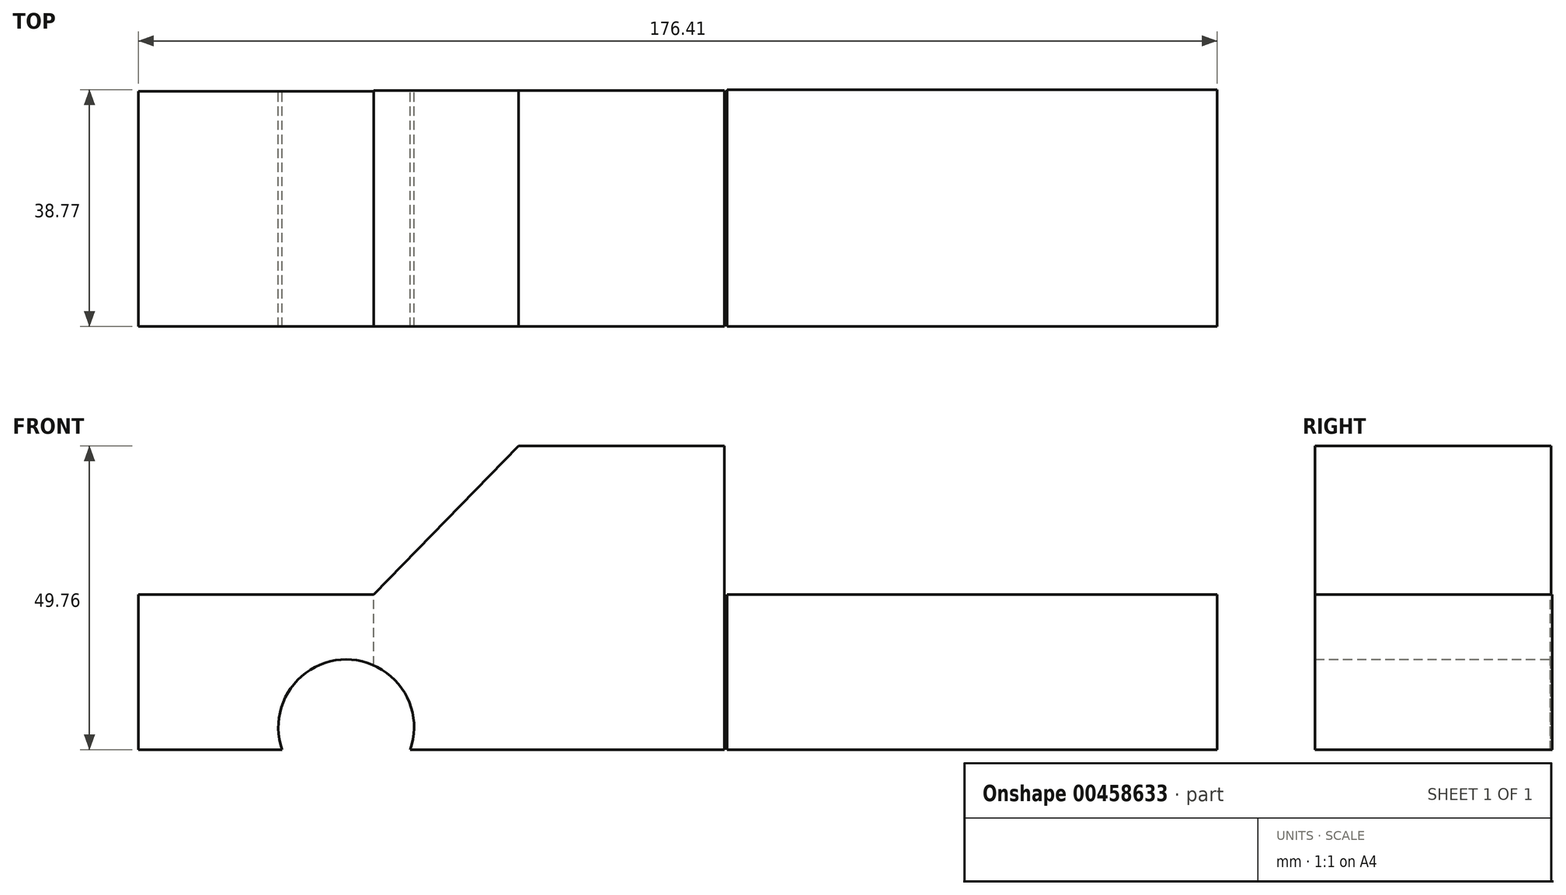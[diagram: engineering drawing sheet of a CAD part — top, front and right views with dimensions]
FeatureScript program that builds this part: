
annotation { "Feature Type Name" : "Feature", "Feature Type Description" : "" }
export const myFeature = defineFeature(function(context is Context, id is Id, definition is map)
    precondition{}
    {
        {
            var Q0;
            Q0=qCreatedBy(makeId("Top.planeOp"),FACE);
            var sketch = newSketch(context, id + "F0", { "sketchPlane" : qUnion([Q0])});
            skLineSegment(sketch, "E0.bottom", {"start": v(-92.4, 18.5) * mm, "end": v(-53.92, 18.5) * mm});
            skLineSegment(sketch, "E0.top", {"start": v(-92.4, -19.97) * mm, "end": v(-53.92, -19.97) * mm});
            skLineSegment(sketch, "E0.left", {"start": v(-92.4, 18.5) * mm, "end": v(-92.4, -19.97) * mm});
            skLineSegment(sketch, "E0.right", {"start": v(-53.92, 18.5) * mm, "end": v(-53.92, -19.97) * mm});
            skSolve(sketch);
        }
        {
            var Q0;
            Q0=makeQuery(id+"F0.imprint","IMPRINT",FACE,{"disambiguationData":[TD([[makeQuery(id+"F0.imprint","IMPRINT",EDGE,{"derivedFrom":sQuery(id+"F0.wireOp",EDGE,"E0.bottom")}),-1.0]])]});
            extrude(context, id + "F1", {"entities" : qUnion([Q0]), "oppositeDirection" : true, "depth" : 25.4 * mm});
        }
        {
            var Q0;
            Q0=makeQuery(id+"F1.opExtrude","SWEPT_FACE",FACE,{"disambiguationData":[OSD([sQuery(id+"F0.wireOp",EDGE,"E0.top")])]});
            var sketch = newSketch(context, id + "F2", { "sketchPlane" : qUnion([Q0])});
            skLineSegment(sketch, "E1.bottom", {"start": v(-53.92, -25.4) * mm, "end": v(3.45, -25.4) * mm});
            skLineSegment(sketch, "E1.top", {"start": v(-30.22, 24.36) * mm, "end": v(3.45, 24.36) * mm});
            skLineSegment(sketch, "E1.left", {"start": v(-53.92, -25.4) * mm, "end": v(-53.92, 0) * mm});
            skLineSegment(sketch, "E1.right", {"start": v(3.45, -25.4) * mm, "end": v(3.45, 24.36) * mm});
            skLineSegment(sketch, "E2", {"start": v(-53.92, 0) * mm, "end": v(-30.22, 24.36) * mm});
            skSolve(sketch);
        }
        {
            var Q0;
            Q0=makeQuery(id+"F2.imprint","IMPRINT",FACE,{"disambiguationData":[TD([[makeQuery(id+"F2.imprint","IMPRINT",EDGE,{"derivedFrom":sQuery(id+"F2.wireOp",EDGE,"E1.bottom")}),1.0]])]});
            extrude(context, id + "F3", {"entities" : qUnion([Q0]), "operationType" : NewBodyOperationType.ADD, "oppositeDirection" : true, "depth" : 38.6 * mm});
        }
        {
            var Q0;
            Q0=qCreatedBy(makeId("Top.planeOp"),FACE);
            var sketch = newSketch(context, id + "F4", { "sketchPlane" : qUnion([Q0])});
            skLineSegment(sketch, "E3.bottom", {"start": v(3.85, 18.8) * mm, "end": v(84, 18.8) * mm});
            skLineSegment(sketch, "E3.top", {"start": v(3.85, -19.97) * mm, "end": v(84, -19.97) * mm});
            skLineSegment(sketch, "E3.left", {"start": v(3.85, 18.8) * mm, "end": v(3.85, -19.97) * mm});
            skLineSegment(sketch, "E3.right", {"start": v(84, 18.8) * mm, "end": v(84, -19.97) * mm});
            skSolve(sketch);
        }
        {
            var Q0;
            Q0=makeQuery(id+"F4.imprint","IMPRINT",FACE,{"disambiguationData":[TD([[makeQuery(id+"F4.imprint","IMPRINT",EDGE,{"derivedFrom":sQuery(id+"F4.wireOp",EDGE,"E3.bottom")}),-1.0]])]});
            extrude(context, id + "F5", {"entities" : qUnion([Q0]), "oppositeDirection" : true, "depth" : 25.4 * mm});
        }
        {
            var Q0;
            Q0=makeQuery(id+"F3.boolean.opBoolean","MERGE",FACE,{"derivedFrom":[makeQuery(id+"F1.opExtrude","SWEPT_FACE",FACE,{"disambiguationData":[OSD([sQuery(id+"F0.wireOp",EDGE,"E0.top")])]}),makeQuery(id+"F3.opExtrude","CAP_FACE",FACE,{"disambiguationData":[OSD([sQuery(id+"F2.wireOp",EDGE,"E1.bottom"),sQuery(id+"F2.wireOp",EDGE,"E1.top"),sQuery(id+"F2.wireOp",EDGE,"E1.left"),sQuery(id+"F2.wireOp",EDGE,"E1.right"),sQuery(id+"F2.wireOp",EDGE,"E2")])],"isStart":true})]});
            var sketch = newSketch(context, id + "F6", { "sketchPlane" : qUnion([Q0])});
            skCircle(sketch, "E4.converted", {"center": v(-58.4, -21.71) * mm, "radius": 11.1 * mm});
            skSolve(sketch);
        }
        {
            var Q0;
            {var subQ0=sQuery(id+"F6.wireOp",EDGE,"E4.converted");var subQ1=makeQuery(id+"F3.boolean.opBoolean","MERGE",EDGE,{"derivedFrom":[makeQuery(id+"F1.opExtrude","CAP_EDGE",EDGE,{"disambiguationData":[OSD([sQuery(id+"F0.wireOp",EDGE,"E0.top")])],"isStart":false}),makeQuery(id+"F3.opExtrude","CAP_EDGE",EDGE,{"disambiguationData":[OSD([sQuery(id+"F2.wireOp",EDGE,"E1.bottom")])],"isStart":true})]});var subQ2=makeQuery(id+"F6.imprint","INTERSECT",VERTEX,{"disambiguationData":[OD(0.0)],"derivedFrom":[subQ1,subQ0]});Q0=makeQuery(id+"F6.imprint","IMPRINT",FACE,{"disambiguationData":[TD([[makeQuery(id+"F6.imprint","IMPRINT",EDGE,{"disambiguationData":[TD([[subQ2,1.0]])],"derivedFrom":subQ0}),1.0]])]});}
            extrude(context, id + "F7", {"entities" : qUnion([Q0]), "operationType" : NewBodyOperationType.REMOVE, "endBound" : BoundingType.THROUGH_ALL, "depth" : 25.4 * mm, "hasSecondDirection" : true, "secondDirectionOppositeDirection" : true, "secondDirectionDepth" : 127 * mm});
        }
    });
